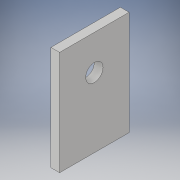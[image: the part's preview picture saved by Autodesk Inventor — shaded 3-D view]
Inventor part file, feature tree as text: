
AUTODESK INVENTOR PART (.ipt)
format: ipt  version: 2017 (Build 210142000, 142)  size: 100,864 bytes
history: native  units: in
note: dims shown in document units (in); Inventor stores cm internally (conversion verified against a paired STEP export)
features: sketch x2, extrude x1, hole x1
ambient origin geometry x8: Origin, YZ Plane, XZ Plane, XY Plane, X Axis, Y Axis, Z Axis, Center Point
bodies: Solid1 (feature_tree)
feature tree (4):
  extrude  "Extrusion1"  Depth=2.0in
  hole  "Hole1"  [1 undecoded]
  sketch  "Sketch1"  dims[d0=3.0in d1=2.0in]
  sketch  "Sketch2"  dims[d2=0.25in d3=0.0in d4=2.0in d5=1.0in d6=1.0in d7=0.5in d8=0.75in d9=0.375in d10=0.25in d11=0.5635in d12=1.0in d13=0.8108in]
note: 1 required parameter value undecoded (feature->parameter linkage not recoverable at this tier; creation-order binding heuristic only, values carry confidence <= 0.55)
